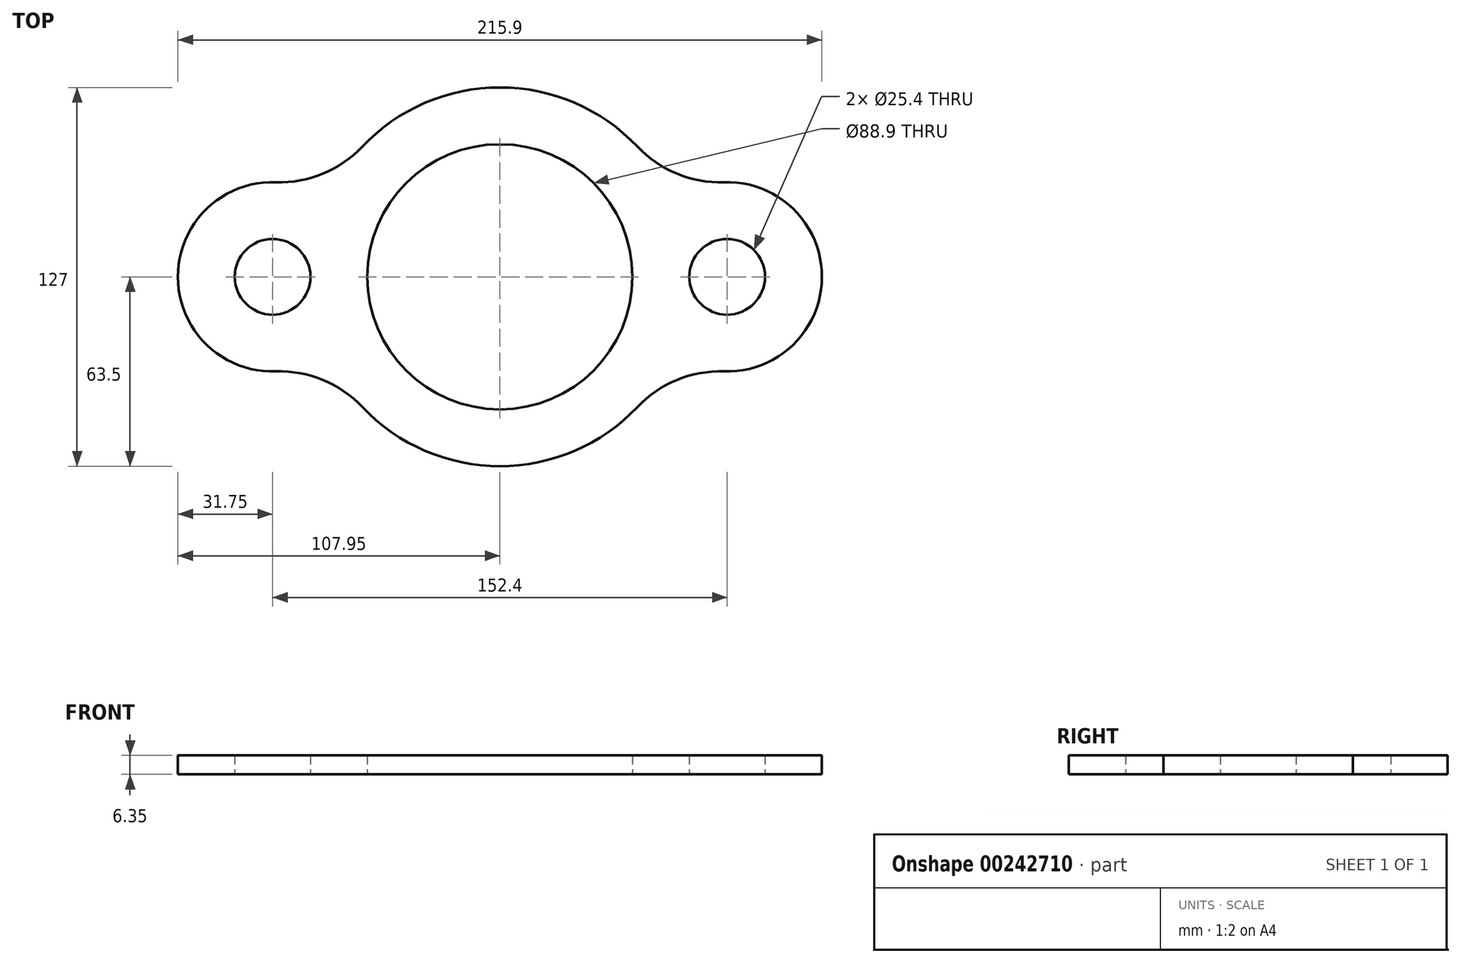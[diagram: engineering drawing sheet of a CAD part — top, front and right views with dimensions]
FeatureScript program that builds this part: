
annotation { "Feature Type Name" : "Feature", "Feature Type Description" : "" }
export const myFeature = defineFeature(function(context is Context, id is Id, definition is map)
    precondition{}
    {
        {
            var Q0;
            Q0=qCreatedBy(makeId("Top.planeOp"),FACE);
            var sketch = newSketch(context, id + "F0", { "sketchPlane" : qUnion([Q0])});
            skArc(sketch, "E0", {"start": v(-46.14, -43.63) * mm, "mid": v(0, -63.5) * mm, "end": v(46.14, -43.63) * mm});
            skCircle(sketch, "E1", {"center": v(0, 0) * mm, "radius": 44.45 * mm});
            skCircle(sketch, "E2", {"center": v(76.2, 0) * mm, "radius": 12.7 * mm});
            skCircle(sketch, "E3", {"center": v(-76.2, 0) * mm, "radius": 12.7 * mm});
            skArc(sketch, "E4", {"start": v(75.12, -31.73) * mm, "mid": v(107.95, 0) * mm, "end": v(75.12, 31.73) * mm});
            skArc(sketch, "E5", {"start": v(-75.12, 31.73) * mm, "mid": v(-107.95, 0) * mm, "end": v(-75.12, -31.73) * mm});
            skLineSegment(sketch, "E6", {"start": v(0, 0) * mm, "end": v(-44.45, 0) * mm});
            skLineSegment(sketch, "E7", {"start": v(0, 0) * mm, "end": v(44.45, 0) * mm});
            skLineSegment(sketch, "E8.trimOffspring", {"start": v(-63.5, 0) * mm, "end": v(-76.2, 0) * mm});
            skArc(sketch, "E9.trimOffspring", {"start": v(46.14, 43.63) * mm, "mid": v(0, 63.5) * mm, "end": v(-46.14, 43.63) * mm});
            skLineSegment(sketch, "E10.trimOffspring", {"start": v(63.5, 0) * mm, "end": v(76.2, 0) * mm});
            skLineSegment(sketch, "E11", {"start": v(0, 0) * mm, "end": v(76.2, 0) * mm});
            skPoint(sketch, "E12.visualSharp", {"position": v(-57.94, 25.98) * mm});
            skArc(sketch, "E12.filletArc", {"start": v(-75.12, 31.73) * mm, "mid": v(-59.35, 34.56) * mm, "end": v(-46.14, 43.63) * mm});
            skPoint(sketch, "E13.visualSharp", {"position": v(57.94, 25.98) * mm});
            skArc(sketch, "E13.filletArc", {"start": v(46.14, 43.63) * mm, "mid": v(59.35, 34.56) * mm, "end": v(75.12, 31.73) * mm});
            skPoint(sketch, "E14.visualSharp", {"position": v(-57.94, -25.98) * mm});
            skArc(sketch, "E14.filletArc", {"start": v(-46.14, -43.63) * mm, "mid": v(-59.35, -34.56) * mm, "end": v(-75.12, -31.73) * mm});
            skPoint(sketch, "E15.visualSharp", {"position": v(57.94, -25.98) * mm});
            skArc(sketch, "E15.filletArc", {"start": v(75.12, -31.73) * mm, "mid": v(59.35, -34.56) * mm, "end": v(46.14, -43.63) * mm});
            skSolve(sketch);
        }
        {
            var Q0;
            Q0=makeQuery(id+"F0.imprint","IMPRINT",FACE,{"disambiguationData":[TD([[makeQuery(id+"F0.imprint","IMPRINT",EDGE,{"derivedFrom":sQuery(id+"F0.wireOp",EDGE,"E0")}),1.0]])]});
            extrude(context, id + "F1", {"entities" : qUnion([Q0]), "depth" : 6.35 * mm});
        }
    });
